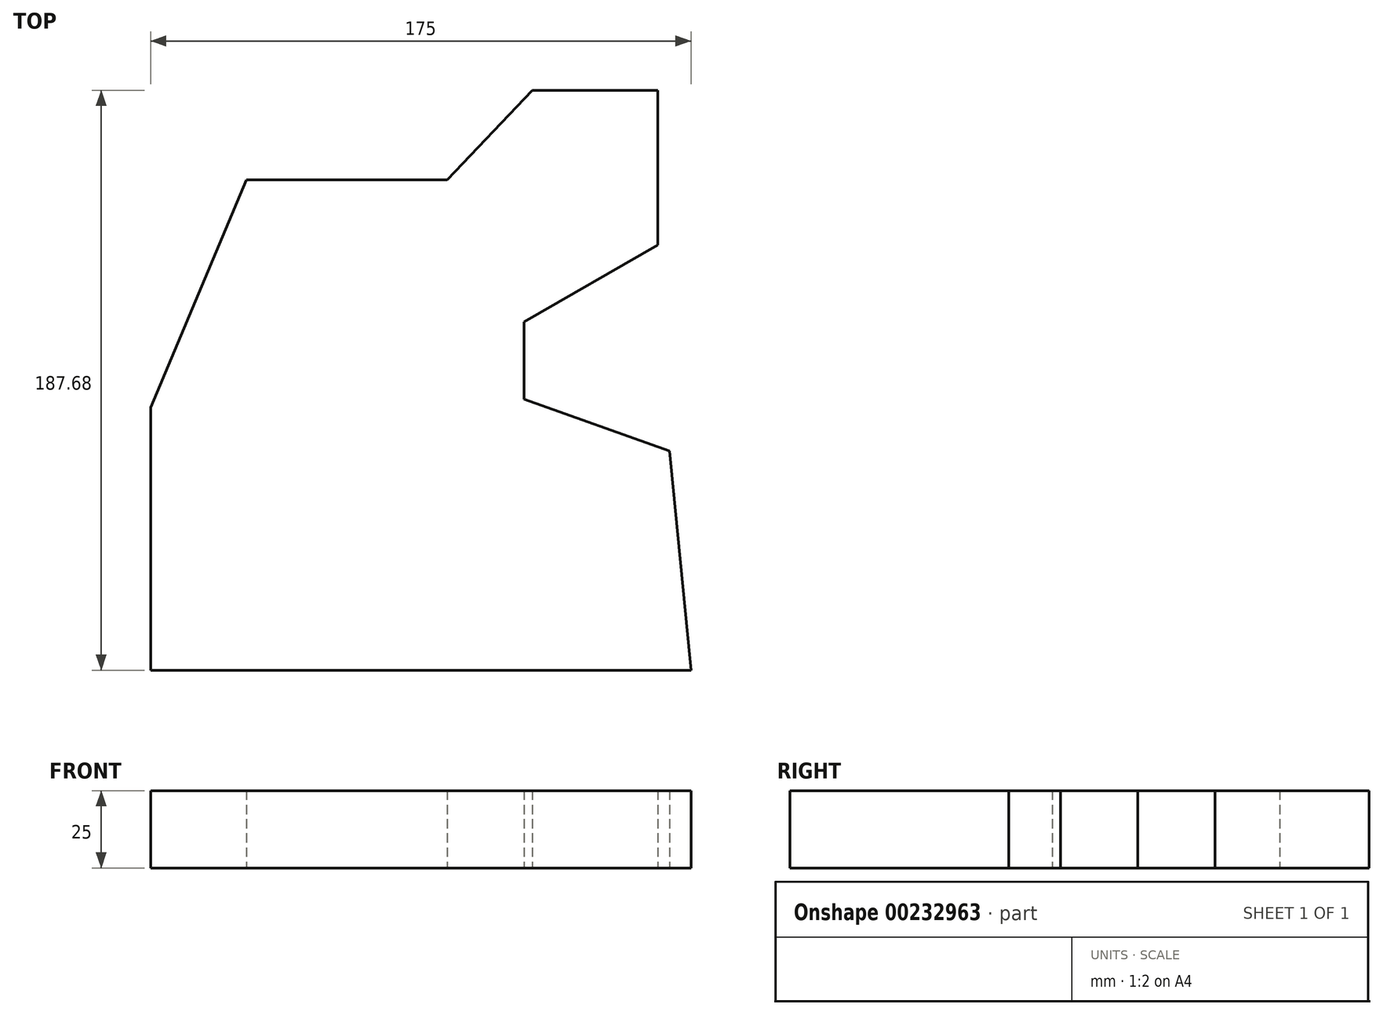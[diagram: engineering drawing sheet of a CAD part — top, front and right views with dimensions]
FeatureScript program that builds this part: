
annotation { "Feature Type Name" : "Feature", "Feature Type Description" : "" }
export const myFeature = defineFeature(function(context is Context, id is Id, definition is map)
    precondition{}
    {
        {
            var Q0;
            Q0=qCreatedBy(makeId("Top.planeOp"),FACE);
            var sketch = newSketch(context, id + "F0", { "sketchPlane" : qUnion([Q0])});
            skLineSegment(sketch, "E0", {"start": v(-96.07, -53.57) * mm, "end": v(78.93, -53.57) * mm});
            skLineSegment(sketch, "E1", {"start": v(-96.07, -53.57) * mm, "end": v(-96.07, 31.43) * mm});
            skLineSegment(sketch, "E2", {"start": v(-96.07, 31.43) * mm, "end": v(-65, 105.16) * mm});
            skLineSegment(sketch, "E3", {"start": v(-65, 105.16) * mm, "end": v(0, 105.16) * mm});
            skLineSegment(sketch, "E4", {"start": v(0, 105.16) * mm, "end": v(27.6, 134.11) * mm});
            skLineSegment(sketch, "E5", {"start": v(27.6, 134.11) * mm, "end": v(68.13, 134.11) * mm});
            skLineSegment(sketch, "E6", {"start": v(68.13, 134.11) * mm, "end": v(68.13, 84.11) * mm});
            skLineSegment(sketch, "E7", {"start": v(68.13, 84.11) * mm, "end": v(24.83, 59.11) * mm});
            skLineSegment(sketch, "E8", {"start": v(24.83, 59.11) * mm, "end": v(24.83, 34.11) * mm});
            skLineSegment(sketch, "E9", {"start": v(24.83, 34.11) * mm, "end": v(71.95, 17.39) * mm});
            skLineSegment(sketch, "E10", {"start": v(24.83, 34.11) * mm, "end": v(54.83, 34.11) * mm});
            skLineSegment(sketch, "E11", {"start": v(24.83, 59.11) * mm, "end": v(82.3, 59.11) * mm});
            skLineSegment(sketch, "E12", {"start": v(71.95, 17.39) * mm, "end": v(78.93, -53.57) * mm});
            skSolve(sketch);
        }
        {
            var Q0;
            Q0 = qSketchRegion(id + "F0", true);
            extrude(context, id + "F1", {"entities" : qUnion([Q0]), "depth" : 25 * mm});
        }
    });
